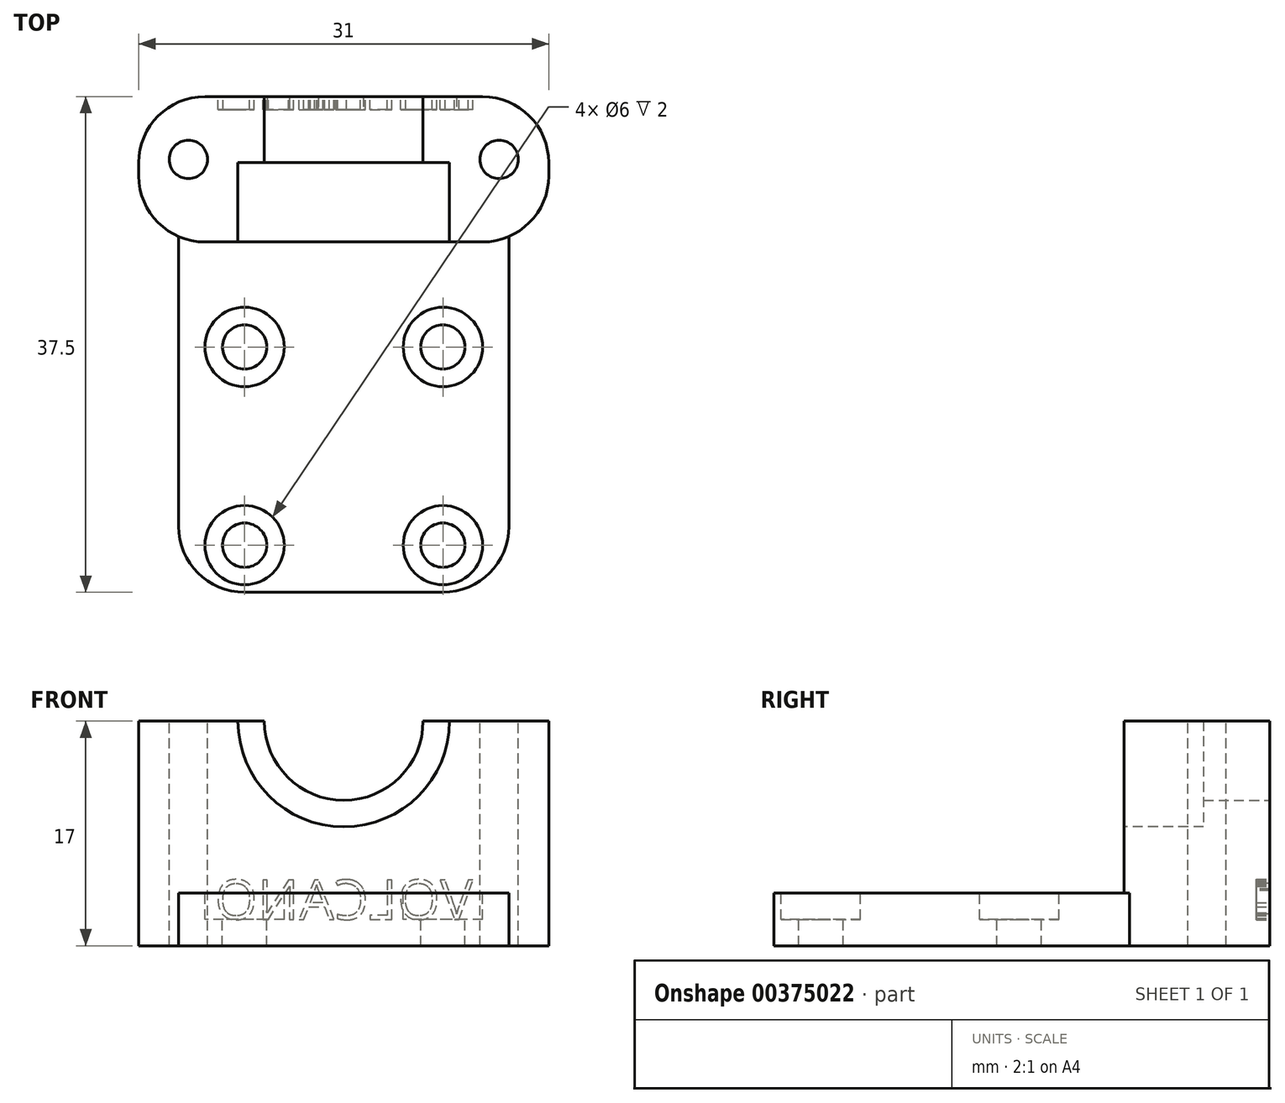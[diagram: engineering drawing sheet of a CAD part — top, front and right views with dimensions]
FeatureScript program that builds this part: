
annotation { "Feature Type Name" : "Feature", "Feature Type Description" : "" }
export const myFeature = defineFeature(function(context is Context, id is Id, definition is map)
    precondition{}
    {
        {
            var Q0;
            Q0=qCreatedBy(makeId("Top.planeOp"),FACE);
            var sketch = newSketch(context, id + "F0", { "sketchPlane" : qUnion([Q0])});
            skLineSegment(sketch, "E0.bottom", {"start": v(0, 0) * mm, "end": v(25, 0) * mm});
            skLineSegment(sketch, "E0.top", {"start": v(0, 30) * mm, "end": v(25, 30) * mm});
            skLineSegment(sketch, "E0.left", {"start": v(0, 0) * mm, "end": v(0, 30) * mm});
            skLineSegment(sketch, "E0.right", {"start": v(25, 0) * mm, "end": v(25, 30) * mm});
            skLineSegment(sketch, "E1.top", {"start": v(0, 37.5) * mm, "end": v(25, 37.5) * mm});
            skLineSegment(sketch, "E1.left", {"start": v(0, 30) * mm, "end": v(0, 37.5) * mm});
            skLineSegment(sketch, "E1.right", {"start": v(25, 30) * mm, "end": v(25, 37.5) * mm});
            skSolve(sketch);
        }
        {
            var Q0;
            Q0=qSketchRegion(id+"F0",true);
            extrude(context, id + "F1", {"entities" : qUnion([Q0]), "depth" : 4 * mm});
        }
        {
            var Q0;
            Q0=makeQuery(id+"F1.opExtrude","CAP_FACE",FACE,{"disambiguationData":[OSD([sQuery(id+"F0.wireOp",EDGE,"E0.bottom"),sQuery(id+"F0.wireOp",EDGE,"E0.top"),sQuery(id+"F0.wireOp",EDGE,"E0.left"),sQuery(id+"F0.wireOp",EDGE,"E0.right")])],"isStart":false});
            var sketch = newSketch(context, id + "F2", { "sketchPlane" : qUnion([Q0])});
            skCircle(sketch, "E2", {"center": v(5, 18.56) * mm, "radius": 1.68 * mm});
            skCircle(sketch, "E3", {"center": v(20, 18.56) * mm, "radius": 1.68 * mm});
            skCircle(sketch, "E4", {"center": v(5, 3.56) * mm, "radius": 1.68 * mm});
            skCircle(sketch, "E5", {"center": v(20, 3.56) * mm, "radius": 1.68 * mm});
            skLineSegment(sketch, "E6", {"start": v(5, 18.56) * mm, "end": v(0, 18.56) * mm});
            skLineSegment(sketch, "E7", {"start": v(20, 3.56) * mm, "end": v(25, 3.56) * mm});
            skCircle(sketch, "E8", {"center": v(5, 18.56) * mm, "radius": 3 * mm});
            skCircle(sketch, "E9", {"center": v(20, 18.56) * mm, "radius": 3 * mm});
            skCircle(sketch, "E10", {"center": v(5, 3.56) * mm, "radius": 3 * mm});
            skCircle(sketch, "E11", {"center": v(20, 3.56) * mm, "radius": 3 * mm});
            skSolve(sketch);
        }
        {
            var Q0;
            Q0=makeQuery(id+"F2.imprint","IMPRINT",FACE,{"disambiguationData":[TD([[makeQuery(id+"F2.imprint","IMPRINT",EDGE,{"derivedFrom":sQuery(id+"F2.wireOp",EDGE,"E2")}),1.0]])]});
            var Q1;
            Q1=makeQuery(id+"F2.imprint","IMPRINT",FACE,{"disambiguationData":[TD([[makeQuery(id+"F2.imprint","IMPRINT",EDGE,{"derivedFrom":sQuery(id+"F2.wireOp",EDGE,"E3")}),1.0]])]});
            var Q2;
            Q2=makeQuery(id+"F2.imprint","IMPRINT",FACE,{"disambiguationData":[TD([[makeQuery(id+"F2.imprint","IMPRINT",EDGE,{"derivedFrom":sQuery(id+"F2.wireOp",EDGE,"E5")}),1.0]])]});
            var Q3;
            Q3=makeQuery(id+"F2.imprint","IMPRINT",FACE,{"disambiguationData":[TD([[makeQuery(id+"F2.imprint","IMPRINT",EDGE,{"derivedFrom":sQuery(id+"F2.wireOp",EDGE,"E4")}),1.0]])]});
            extrude(context, id + "F3", {"entities" : qUnion([Q0, Q1, Q2, Q3]), "operationType" : NewBodyOperationType.REMOVE, "oppositeDirection" : true, "depth" : 25 * mm});
        }
        {
            var Q0;
            Q0=makeQuery(id+"F1.opExtrude","CAP_FACE",FACE,{"disambiguationData":[OSD([sQuery(id+"F0.wireOp",EDGE,"E0.bottom"),sQuery(id+"F0.wireOp",EDGE,"E0.top"),sQuery(id+"F0.wireOp",EDGE,"E0.left"),sQuery(id+"F0.wireOp",EDGE,"E0.right")])],"isStart":false});
            var sketch = newSketch(context, id + "F4", { "sketchPlane" : qUnion([Q0])});
            skLineSegment(sketch, "E12.bottom", {"start": v(0, 37.5) * mm, "end": v(25, 37.5) * mm});
            skLineSegment(sketch, "E12.top", {"start": v(0, 26.5) * mm, "end": v(25, 26.5) * mm});
            skLineSegment(sketch, "E12.left", {"start": v(0, 37.5) * mm, "end": v(0, 26.5) * mm});
            skLineSegment(sketch, "E12.right", {"start": v(25, 37.5) * mm, "end": v(25, 26.5) * mm});
            skSolve(sketch);
        }
        {
            var Q0;
            Q0=qSketchRegion(id+"F4",true);
            extrude(context, id + "F5", {"entities" : qUnion([Q0]), "operationType" : NewBodyOperationType.ADD, "depth" : 13 * mm});
        }
        {
            var Q0;
            Q0=makeQuery(id+"F5.boolean.opBoolean","MERGE",FACE,{"derivedFrom":[makeQuery(id+"F1.opExtrude","SWEPT_FACE",FACE,{"disambiguationData":[OSD([sQuery(id+"F0.wireOp",EDGE,"E1.top")])]}),makeQuery(id+"F5.opExtrude","SWEPT_FACE",FACE,{"disambiguationData":[OSD([sQuery(id+"F4.wireOp",EDGE,"E12.bottom")])]})]});
            var sketch = newSketch(context, id + "F6", { "sketchPlane" : qUnion([Q0])});
            skCircle(sketch, "E13", {"center": v(-12.5, 17) * mm, "radius": 6 * mm});
            skSolve(sketch);
        }
        {
            var Q0;
            {var subQ0=makeQuery(id+"F5.opExtrude","CAP_EDGE",EDGE,{"disambiguationData":[OSD([sQuery(id+"F4.wireOp",EDGE,"3fca9e3f-73a0-4211-9b6f-f3487c54c975.bottom")])],"isStart":false});var subQ1=sQuery(id+"F6.wireOp",EDGE,"E13");var subQ3=makeQuery(id+"F6.imprint","INTERSECT",VERTEX,{"disambiguationData":[OD(0.0)],"derivedFrom":[subQ0,subQ1]});Q0=makeQuery(id+"F6.imprint","IMPRINT",FACE,{"disambiguationData":[TD([[makeQuery(id+"F6.imprint","IMPRINT",EDGE,{"disambiguationData":[TD([[subQ3,1.0]])],"derivedFrom":subQ1}),1.0]])]});}
            var Q1;
            {var subQ0=sQuery(id+"F6.wireOp",EDGE,"E13");var subQ1=makeQuery(id+"F5.opExtrude","CAP_EDGE",EDGE,{"disambiguationData":[OSD([sQuery(id+"F4.wireOp",EDGE,"E12.top")])],"isStart":false});var subQ2=makeQuery(id+"F6.imprint","INTERSECT",VERTEX,{"disambiguationData":[OD(0.0)],"derivedFrom":[subQ1,subQ0]});Q1=makeQuery(id+"F6.imprint","IMPRINT",FACE,{"disambiguationData":[TD([[makeQuery(id+"F6.imprint","IMPRINT",EDGE,{"disambiguationData":[TD([[subQ2,-1.0]])],"derivedFrom":subQ0}),1.0]])]});}
            extrude(context, id + "F7", {"entities" : qUnion([Q0, Q1]), "operationType" : NewBodyOperationType.REMOVE, "oppositeDirection" : true, "depth" : 6 * mm});
        }
        {
            var Q0;
            Q0=makeQuery(id+"F5.opExtrude","SWEPT_FACE",FACE,{"disambiguationData":[OSD([sQuery(id+"F4.wireOp",EDGE,"E12.top")])]});
            var sketch = newSketch(context, id + "F8", { "sketchPlane" : qUnion([Q0])});
            skCircle(sketch, "E14", {"center": v(12.5, 17) * mm, "radius": 8 * mm});
            skSolve(sketch);
        }
        {
            var Q0;
            Q0=qSketchRegion(id+"F8",true);
            extrude(context, id + "F9", {"entities" : qUnion([Q0]), "operationType" : NewBodyOperationType.REMOVE, "oppositeDirection" : true, "depth" : 6 * mm});
        }
        {
            var Q0;
            Q0=makeQuery(id+"F2.imprint","IMPRINT",FACE,{"disambiguationData":[TD([[makeQuery(id+"F2.imprint","IMPRINT",EDGE,{"derivedFrom":sQuery(id+"F2.wireOp",EDGE,"E2")}),-1.0]])]});
            var Q1;
            Q1=makeQuery(id+"F2.imprint","IMPRINT",FACE,{"disambiguationData":[TD([[makeQuery(id+"F2.imprint","IMPRINT",EDGE,{"derivedFrom":sQuery(id+"F2.wireOp",EDGE,"E3")}),-1.0]])]});
            var Q2;
            Q2=makeQuery(id+"F2.imprint","IMPRINT",FACE,{"disambiguationData":[TD([[makeQuery(id+"F2.imprint","IMPRINT",EDGE,{"derivedFrom":sQuery(id+"F2.wireOp",EDGE,"E5")}),-1.0]])]});
            var Q3;
            Q3=makeQuery(id+"F2.imprint","IMPRINT",FACE,{"disambiguationData":[TD([[makeQuery(id+"F2.imprint","IMPRINT",EDGE,{"derivedFrom":sQuery(id+"F2.wireOp",EDGE,"E4")}),-1.0]])]});
            extrude(context, id + "F10", {"entities" : qUnion([Q0, Q1, Q2, Q3]), "operationType" : NewBodyOperationType.REMOVE, "oppositeDirection" : true, "depth" : 2 * mm});
        }
        {
            var Q0;
            Q0=makeQuery(id+"F5.boolean.opBoolean","MERGE",FACE,{"derivedFrom":[makeQuery(id+"F1.opExtrude","SWEPT_FACE",FACE,{"disambiguationData":[OSD([sQuery(id+"F0.wireOp",EDGE,"E0.left")])]}),makeQuery(id+"F5.opExtrude","SWEPT_FACE",FACE,{"disambiguationData":[OSD([sQuery(id+"F4.wireOp",EDGE,"3fca9e3f-73a0-4211-9b6f-f3487c54c975.left")])]})]});
            var sketch = newSketch(context, id + "F11", { "sketchPlane" : qUnion([Q0])});
            skLineSegment(sketch, "E15.bottom", {"start": v(-37.5, 0) * mm, "end": v(-26.5, 0) * mm});
            skLineSegment(sketch, "E15.top", {"start": v(-37.5, 17) * mm, "end": v(-26.5, 17) * mm});
            skLineSegment(sketch, "E15.left", {"start": v(-37.5, 0) * mm, "end": v(-37.5, 17) * mm});
            skLineSegment(sketch, "E15.right", {"start": v(-26.5, 0) * mm, "end": v(-26.5, 17) * mm});
            skSolve(sketch);
        }
        {
            var Q0;
            Q0=qSketchRegion(id+"F11",true);
            extrude(context, id + "F12", {"entities" : qUnion([Q0]), "operationType" : NewBodyOperationType.ADD, "depth" : 3 * mm});
        }
        {
            var Q0;
            Q0=makeQuery(id+"F5.boolean.opBoolean","MERGE",FACE,{"derivedFrom":[makeQuery(id+"F1.opExtrude","SWEPT_FACE",FACE,{"disambiguationData":[OSD([sQuery(id+"F0.wireOp",EDGE,"E0.right")])]}),makeQuery(id+"F5.opExtrude","SWEPT_FACE",FACE,{"disambiguationData":[OSD([sQuery(id+"F4.wireOp",EDGE,"3fca9e3f-73a0-4211-9b6f-f3487c54c975.right")])]})]});
            var sketch = newSketch(context, id + "F13", { "sketchPlane" : qUnion([Q0])});
            skLineSegment(sketch, "E16.bottom", {"start": v(37.5, 17) * mm, "end": v(26.5, 17) * mm});
            skLineSegment(sketch, "E16.top", {"start": v(37.5, 0) * mm, "end": v(26.5, 0) * mm});
            skLineSegment(sketch, "E16.left", {"start": v(37.5, 17) * mm, "end": v(37.5, 0) * mm});
            skLineSegment(sketch, "E16.right", {"start": v(26.5, 17) * mm, "end": v(26.5, 0) * mm});
            skSolve(sketch);
        }
        {
            var Q0;
            Q0=qSketchRegion(id+"F13",true);
            extrude(context, id + "F14", {"entities" : qUnion([Q0]), "operationType" : NewBodyOperationType.ADD, "depth" : 3 * mm});
        }
        {
            var Q0;
            {var subQ0=sQuery(id+"F4.wireOp",EDGE,"E12.bottom");var subQ1=sQuery(id+"F4.wireOp",EDGE,"E12.top");var subQ3=sQuery(id+"F4.wireOp",EDGE,"E12.right");Q0=makeQuery(id+"F14.boolean.opBoolean","MERGE",FACE,{"derivedFrom":[makeQuery(id+"F9.boolean.opBoolean","SPLIT",FACE,{"disambiguationData":[TD([makeQuery(id+"F5.opExtrude","SWEPT_FACE",FACE,{"disambiguationData":[OSD([subQ3])]})])],"derivedFrom":makeQuery(id+"F5.opExtrude","CAP_FACE",FACE,{"disambiguationData":[OSD([subQ0,subQ1,sQuery(id+"F4.wireOp",EDGE,"E12.left"),subQ3])],"isStart":false})}),makeQuery(id+"F14.opExtrude","SWEPT_FACE",FACE,{"disambiguationData":[OSD([sQuery(id+"F13.wireOp",EDGE,"E16.bottom")])]})]});}
            var sketch = newSketch(context, id + "F15", { "sketchPlane" : qUnion([Q0])});
            skCircle(sketch, "E17", {"center": v(0.75, 32.75) * mm, "radius": 1.45 * mm});
            skCircle(sketch, "E18", {"center": v(24.25, 32.75) * mm, "radius": 1.45 * mm});
            skSolve(sketch);
        }
        {
            var Q0;
            Q0=qSketchRegion(id+"F15",true);
            extrude(context, id + "F16", {"entities" : qUnion([Q0]), "operationType" : NewBodyOperationType.REMOVE, "oppositeDirection" : true, "depth" : 25 * mm});
        }
        {
            var Q0;
            Q0=makeQuery(id+"F12.opExtrude","CAP_EDGE",EDGE,{"disambiguationData":[OSD([sQuery(id+"F11.wireOp",EDGE,"E15.left")])],"isStart":false});
            var Q1;
            Q1=makeQuery(id+"F12.opExtrude","CAP_EDGE",EDGE,{"disambiguationData":[OSD([sQuery(id+"F11.wireOp",EDGE,"E15.right")])],"isStart":false});
            var Q2;
            Q2=makeQuery(id+"F14.opExtrude","CAP_EDGE",EDGE,{"disambiguationData":[OSD([sQuery(id+"F13.wireOp",EDGE,"E16.right")])],"isStart":false});
            var Q3;
            Q3=makeQuery(id+"F14.opExtrude","CAP_EDGE",EDGE,{"disambiguationData":[OSD([sQuery(id+"F13.wireOp",EDGE,"E16.left")])],"isStart":false});
            var Q4;
            Q4=makeQuery(id+"F1.opExtrude","SWEPT_EDGE",EDGE,{"disambiguationData":[OSD([sQuery(id+"F0.wireOp",EDGE,"E0.bottom"),sQuery(id+"F0.wireOp",EDGE,"E0.right")])]});
            var Q5;
            Q5=makeQuery(id+"F1.opExtrude","SWEPT_EDGE",EDGE,{"disambiguationData":[OSD([sQuery(id+"F0.wireOp",EDGE,"E0.bottom"),sQuery(id+"F0.wireOp",EDGE,"E0.left")])]});
            fillet(context, id + "F17", {"entities" : qUnion([Q0, Q1, Q2, Q3, Q4, Q5]), "radius" : 5 * mm, "tangentPropagation" : true, "allowEdgeOverflow" : false});
        }
        {
            var Q0;
            Q0=makeQuery(id+"F2.imprint","IMPRINT",FACE,{"disambiguationData":[TD([[makeQuery(id+"F2.imprint","IMPRINT",EDGE,{"derivedFrom":sQuery(id+"F2.wireOp",EDGE,"E2")}),-1.0]])]});
            var Q1;
            Q1=makeQuery(id+"F2.imprint","IMPRINT",FACE,{"disambiguationData":[TD([[makeQuery(id+"F2.imprint","IMPRINT",EDGE,{"derivedFrom":sQuery(id+"F2.wireOp",EDGE,"E3")}),-1.0]])]});
            var Q2;
            Q2=makeQuery(id+"F2.imprint","IMPRINT",FACE,{"disambiguationData":[TD([[makeQuery(id+"F2.imprint","IMPRINT",EDGE,{"derivedFrom":sQuery(id+"F2.wireOp",EDGE,"E2")}),1.0]])]});
            var Q3;
            Q3=makeQuery(id+"F2.imprint","IMPRINT",FACE,{"disambiguationData":[TD([[makeQuery(id+"F2.imprint","IMPRINT",EDGE,{"derivedFrom":sQuery(id+"F2.wireOp",EDGE,"E3")}),1.0]])]});
            extrude(context, id + "F18", {"entities" : qUnion([Q0, Q1, Q2, Q3]), "operationType" : NewBodyOperationType.REMOVE, "depth" : 25 * mm});
        }
        {
            var Q0;
            Q0=makeQuery(id+"F14.boolean.opBoolean","MERGE",FACE,{"derivedFrom":[makeQuery(id+"F12.boolean.opBoolean","MERGE",FACE,{"derivedFrom":[makeQuery(id+"F5.boolean.opBoolean","MERGE",FACE,{"derivedFrom":[makeQuery(id+"F1.opExtrude","SWEPT_FACE",FACE,{"disambiguationData":[OSD([sQuery(id+"F0.wireOp",EDGE,"E1.top")])]}),makeQuery(id+"F5.opExtrude","SWEPT_FACE",FACE,{"disambiguationData":[OSD([sQuery(id+"F4.wireOp",EDGE,"E12.bottom")])]})]}),makeQuery(id+"F12.opExtrude","SWEPT_FACE",FACE,{"disambiguationData":[OSD([sQuery(id+"F11.wireOp",EDGE,"E15.left")])]})]}),makeQuery(id+"F14.opExtrude","SWEPT_FACE",FACE,{"disambiguationData":[OSD([sQuery(id+"F13.wireOp",EDGE,"E16.left")])]})]});
            var sketch = newSketch(context, id + "F19", { "sketchPlane" : qUnion([Q0])});
            skText(sketch, "E19", { "text": "VOLCANO", "fontName": "OpenSans-Regular.ttf"});
            const initialGuessF19  = {"E19": [-0.02228, 0.002, 1, 0, 0.003]};
            skSetInitialGuess(sketch, initialGuessF19);
            skSolve(sketch);
        }
        {
            var Q0;
            Q0=qSketchRegion(id+"F19",true);
            extrude(context, id + "F20", {"entities" : qUnion([Q0]), "operationType" : NewBodyOperationType.REMOVE, "oppositeDirection" : true, "depth" : 1 * mm});
        }
    });
